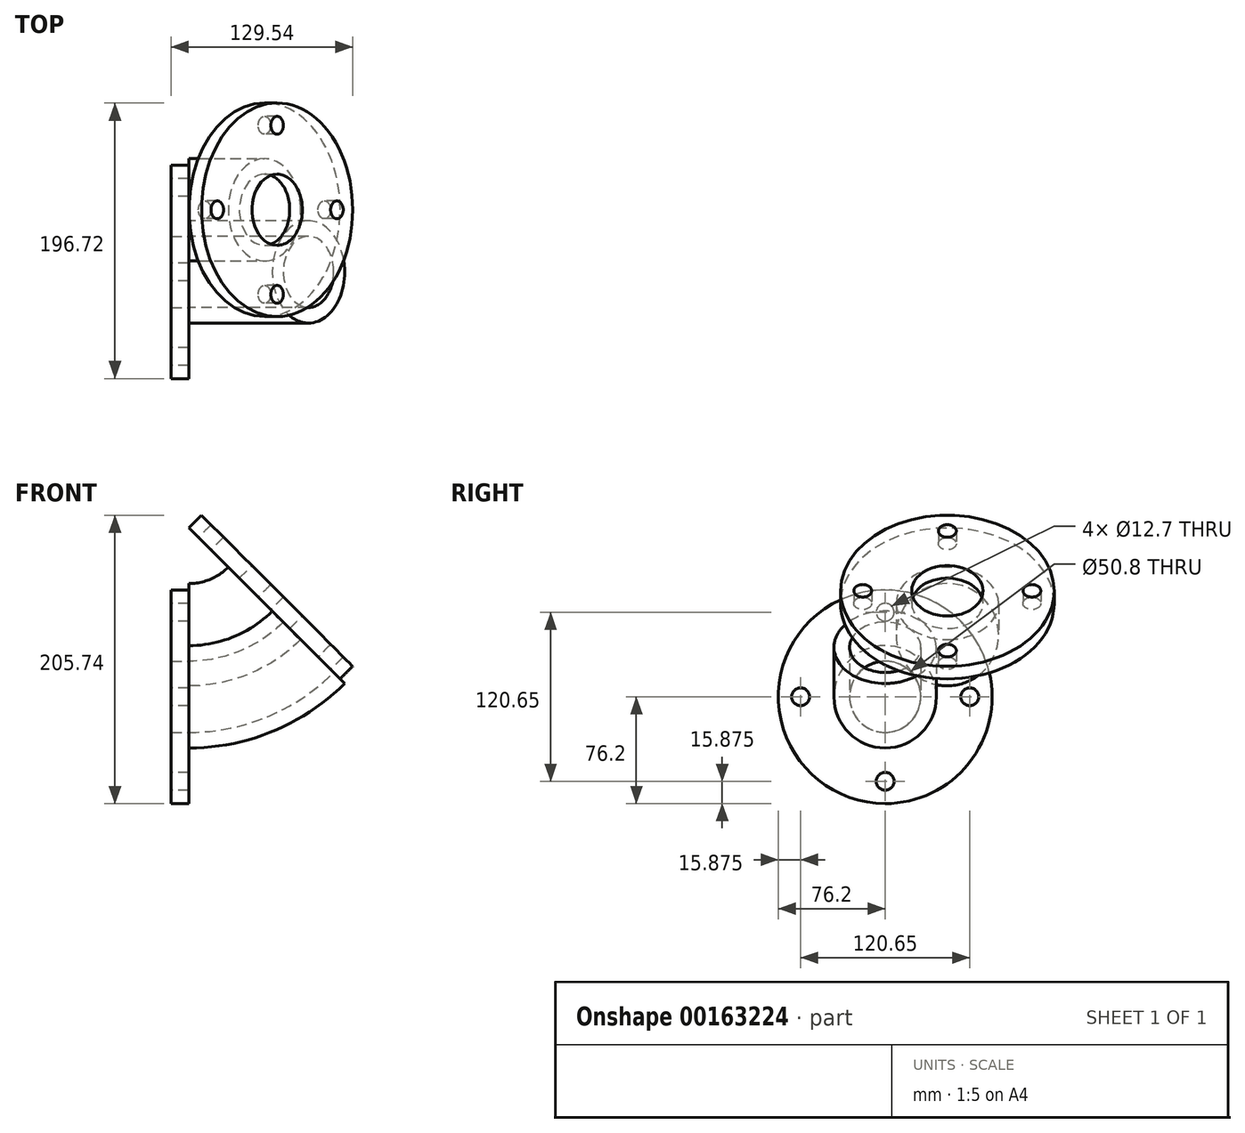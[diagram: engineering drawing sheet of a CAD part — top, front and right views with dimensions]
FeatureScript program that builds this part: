
annotation { "Feature Type Name" : "Feature", "Feature Type Description" : "" }
export const myFeature = defineFeature(function(context is Context, id is Id, definition is map)
    precondition{}
    {
        {
            var Q0;
            Q0=qCreatedBy(makeId("Right.planeOp"),FACE);
            var sketch = newSketch(context, id + "F0", { "sketchPlane" : qUnion([Q0])});
            skCircle(sketch, "E0", {"center": v(0, 0) * mm, "radius": 60.33 * mm, "construction": true});
            skPoint(sketch, "E1", {"position": v(0, 60.33) * mm});
            skPoint(sketch, "E2", {"position": v(60.33, 0) * mm});
            skPoint(sketch, "E3", {"position": v(0, -60.33) * mm});
            skPoint(sketch, "E4", {"position": v(-60.33, 0) * mm});
            skCircle(sketch, "E5", {"center": v(0, 0) * mm, "radius": 76.2 * mm});
            skSolve(sketch);
        }
        {
            var Q0;
            Q0=makeQuery(id+"F0.imprint","IMPRINT",FACE,{"disambiguationData":[TD([[makeQuery(id+"F0.imprint","IMPRINT",EDGE,{"derivedFrom":sQuery(id+"F0.wireOp",EDGE,"E5")}),1.0]])]});
            extrude(context, id + "F1", {"entities" : qUnion([Q0]), "depth" : 12.7 * mm});
        }
        {
            var Q0;
            Q0=sQuery(id+"F0.wireOp",VERTEX,"E1");
            var Q1;
            Q1=sQuery(id+"F0.wireOp",VERTEX,"E4");
            var Q2;
            Q2=sQuery(id+"F0.wireOp",VERTEX,"E3");
            var Q3;
            Q3=sQuery(id+"F0.wireOp",VERTEX,"E2");
            var Q4;
            Q4=makeQuery(id+"F1.opExtrude","SWEPT_BODY",BODY,{"disambiguationData":[OSD([sQuery(id+"F0.wireOp",EDGE,"E5")])]});
            hole(context, id + "F2", {"style" : HoleStyle.SIMPLE, "endStyle" : HoleEndStyle.THROUGH, "oppositeDirection" : true, "holeDiameter" : 12.7 * mm, "locations" : qUnion([Q0, Q1, Q2, Q3]), "scope" : qUnion([Q4]), "isTappedThrough" : true});
        }
        {
            var Q0;
            Q0=qCreatedBy(makeId("Front.planeOp"),FACE);
            var sketch = newSketch(context, id + "F3", { "sketchPlane" : qUnion([Q0])});
            skLineSegment(sketch, "E6.0", {"start": v(12.7, 76.2) * mm, "end": v(12.7, -76.2) * mm});
            skArc(sketch, "E7", {"start": v(12.7, 0) * mm, "mid": v(58.87, 9.18) * mm, "end": v(98.01, 35.34) * mm});
            skLineSegment(sketch, "E8", {"start": v(98.01, 35.34) * mm, "end": v(124.68, 62) * mm, "construction": true});
            skLineSegment(sketch, "E9", {"start": v(98.01, 35.34) * mm, "end": v(136.58, -3.23) * mm, "construction": true});
            skLineSegment(sketch, "E10", {"start": v(12.7, 0) * mm, "end": v(-54.09, 0) * mm, "construction": true});
            skArc(sketch, "E11.0", {"start": v(12.7, -36.51) * mm, "mid": v(72.84, -24.55) * mm, "end": v(123.83, 9.52) * mm});
            skArc(sketch, "E12.0", {"start": v(12.7, -25.4) * mm, "mid": v(68.6, -14.28) * mm, "end": v(115.97, 17.38) * mm});
            skSolve(sketch);
        }
        {
            var Q0;
            Q0=makeQuery(id+"F1.opExtrude","CAP_FACE",FACE,{"disambiguationData":[OSD([sQuery(id+"F0.wireOp",EDGE,"E5")])],"isStart":false});
            var sketch = newSketch(context, id + "F4", { "sketchPlane" : qUnion([Q0])});
            skCircle(sketch, "E13", {"center": v(0, 0) * mm, "radius": 36.51 * mm});
            skCircle(sketch, "E14", {"center": v(0, 0) * mm, "radius": 25.4 * mm});
            skSolve(sketch);
        }
        {
            var Q0;
            Q0=sQuery(id+"F3.wireOp",EDGE,"E8");
            var Q1;
            Q1=sQuery(id+"F3.wireOp",VERTEX,"E9.start");
            cPlane(context, id + "F5", {"entities" : qUnion([Q0, Q1]), "cplaneType" : CPlaneType.LINE_POINT, "offset" : 25.4 * mm, "width" : 152.4 * mm, "height" : 152.4 * mm});
        }
        {
            var Q0;
            Q0=qCreatedBy(id+"F5.planeOp",FACE);
            var sketch = newSketch(context, id + "F6", { "sketchPlane" : qUnion([Q0])});
            skCircle(sketch, "E15", {"center": v(44.32, 0) * mm, "radius": 76.2 * mm});
            skCircle(sketch, "E16", {"center": v(44.32, 0) * mm, "radius": 36.51 * mm});
            skCircle(sketch, "E17", {"center": v(44.32, 0) * mm, "radius": 60.33 * mm, "construction": true});
            skPoint(sketch, "E18", {"position": v(-16, 0) * mm});
            skPoint(sketch, "E19", {"position": v(44.32, 60.33) * mm});
            skPoint(sketch, "E20", {"position": v(44.32, -60.33) * mm});
            skPoint(sketch, "E21", {"position": v(104.64, 0) * mm});
            skSolve(sketch);
        }
        {
            var Q0;
            Q0=makeQuery(id+"F4.imprint","IMPRINT",FACE,{"disambiguationData":[TD([[makeQuery(id+"F4.imprint","IMPRINT",EDGE,{"derivedFrom":sQuery(id+"F4.wireOp",EDGE,"E13")}),1.0]])]});
            var Q1;
            Q1=makeQuery(id+"F6.imprint","IMPRINT",FACE,{"disambiguationData":[TD([[makeQuery(id+"F6.imprint","IMPRINT",EDGE,{"derivedFrom":sQuery(id+"F6.wireOp",EDGE,"E16")}),1.0]])]});
            var Q2;
            Q2=sQuery(id+"F3.wireOp",EDGE,"E7");
            sweep(context, id + "F7", {"profiles" : qUnion([Q0, Q1]), "path" : qUnion([Q2])});
        }
        {
            var Q0;
            Q0=makeQuery(id+"F6.imprint","IMPRINT",FACE,{"disambiguationData":[TD([[makeQuery(id+"F6.imprint","IMPRINT",EDGE,{"derivedFrom":sQuery(id+"F6.wireOp",EDGE,"E15")}),1.0]])]});
            var Q1;
            Q1=makeQuery(id+"F6.imprint","IMPRINT",FACE,{"disambiguationData":[TD([[makeQuery(id+"F6.imprint","IMPRINT",EDGE,{"derivedFrom":sQuery(id+"F6.wireOp",EDGE,"E16")}),1.0]])]});
            extrude(context, id + "F8", {"entities" : qUnion([Q0, Q1]), "depth" : 12.7 * mm});
        }
        {
            var Q0;
            Q0=sQuery(id+"F6.wireOp",VERTEX,"E18");
            var Q1;
            Q1=sQuery(id+"F6.wireOp",VERTEX,"E20");
            var Q2;
            Q2=sQuery(id+"F6.wireOp",VERTEX,"E21");
            var Q3;
            Q3=sQuery(id+"F6.wireOp",VERTEX,"E19");
            var Q4;
            Q4=makeQuery(id+"F8.opExtrude","SWEPT_BODY",BODY,{"disambiguationData":[OSD([sQuery(id+"F6.wireOp",EDGE,"E15")])]});
            hole(context, id + "F9", {"style" : HoleStyle.SIMPLE, "endStyle" : HoleEndStyle.THROUGH, "oppositeDirection" : true, "holeDiameter" : 12.7 * mm, "locations" : qUnion([Q0, Q1, Q2, Q3]), "scope" : qUnion([Q4]), "isTappedThrough" : true});
        }
        {
            var Q0;
            Q0=makeQuery(id+"F8.opExtrude","CAP_FACE",FACE,{"disambiguationData":[OSD([sQuery(id+"F6.wireOp",EDGE,"E15")])],"isStart":false});
            var sketch = newSketch(context, id + "F10", { "sketchPlane" : qUnion([Q0])});
            skCircle(sketch, "E22.0", {"center": v(44.32, 0) * mm, "radius": 25.4 * mm});
            skSolve(sketch);
        }
        {
            var Q0;
            Q0=makeQuery(id+"F10.imprint","IMPRINT",FACE,{"disambiguationData":[TD([[makeQuery(id+"F10.imprint","IMPRINT",EDGE,{"derivedFrom":sQuery(id+"F10.wireOp",EDGE,"E22.0")}),1.0]])]});
            extrude(context, id + "F11", {"entities" : qUnion([Q0]), "operationType" : NewBodyOperationType.REMOVE, "oppositeDirection" : true, "depth" : 12.7 * mm});
        }
        {
            var Q0;
            Q0=makeQuery(id+"F4.imprint","IMPRINT",FACE,{"disambiguationData":[TD([[makeQuery(id+"F4.imprint","IMPRINT",EDGE,{"derivedFrom":sQuery(id+"F4.wireOp",EDGE,"E14")}),1.0]])]});
            var Q1;
            Q1=sQuery(id+"F4.wireOp",EDGE,"E14");
            extrude(context, id + "F12", {"entities" : qUnion([Q0]), "operationType" : NewBodyOperationType.REMOVE, "surfaceEntities" : qUnion([Q1]), "endBound" : BoundingType.THROUGH_ALL, "oppositeDirection" : true, "depth" : 25.4 * mm});
        }
    });
